# Revit family: ЭВАН PRACTIC 3-28 кВт
name_source: partatom
category: Оборудование
units: mm (PartAtom-declared; Revit-internal decimal feet)

## family parameters
Всегда вертикально = Да
Классификация = Нет
На основе рабочей плоскости = Да
Общий = Нет
При загрузке вырезать с полостями = Нет
Размер круглого соединителя = Использовать диаметр
Тип детали = Нормальный
Точка расчета площади = Нет

## types (14) — shared parameters
ADSK_Классификация нагрузок = Прочее
ADSK_Материал = Сталь
ADSK_Размер_Высота = 600 мм
ADSK_Размер_Длина = 372 мм
ADSK_Размер_Ширина = 212 мм
ADSK_Расход теплоносителя = 0.0 м³/ч
Dn = 32 мм
База = ЭЛЕКТРИЧЕСКИЙ ТЕПЛОГЕНЕРАТОР (КОТЕЛ)
Диапазон регулируемых температур теплоносителя, оС = От +10 до +85
Максимальная температура теплоносителя, оС = +85
Материал корпуса = Сталь
Минимальная температура теплоносителя, оС = +10
Рабочее давление, МПа = 0,07-0,32
Резьба патрубков для подключения трубопроводов теплоносителя = G1 1/4
zero-valued in all types: Отметка по умолчанию

## per-type parameters (varying)
| type | ADSK_Количество фаз | ADSK_Номинальная мощность | Объем колбы котла, л | Потребляемая электрическая мощность при максимальной тепловой мощность  в час, кВт/ч |
| ЭВАН PRACTIC 3 кВт 380В | 3 | 3000 Вт | 8 | 3.2 |
| ЭВАН PRACTIC 3 кВт 220В | 1 | 3000 Вт | 8 | 3.2 |
| ЭВАН PRACTIC 7 кВт 220В | 1 | 7000 Вт | 8 | 7.3 |
| ЭВАН PRACTIC 5 кВт 380В | 3 | 5000 Вт | 8 | 5.2 |
| ЭВАН PRACTIC 7 кВт 380В | 3 | 7000 Вт | 8 | 7.3 |
| ЭВАН PRACTIC 9 кВт 380В | 3 | 9000 Вт | 8 | 9.3 |
| ЭВАН PRACTIC 9 кВт 220В | 1 | 9000 Вт | 8 | 9.3 |
| ЭВАН PRACTIC 12 кВт | 3 | 12000 Вт | 7,5 | 12.6 |
| ЭВАН PRACTIC 14 кВт | 3 | 14000 Вт | 7,5 | 14.7 |
| ЭВАН PRACTIC 18 кВт | 3 | 18000 Вт | 7,5 | 18.9 |
| ЭВАН PRACTIC 21 кВт | 3 | 21000 Вт | 7,5 | 22.1 |
| ЭВАН PRACTIC 24 кВт | 3 | 24000 Вт | 7,5 | 25.2 |
| ЭВАН PRACTIC 28 кВт | 3 | 28000 Вт | 7,5 | 29.4 |
| ЭВАН PRACTIC 5 кВт 220В | 1 | 5000 Вт | 8 | 5.2 |
